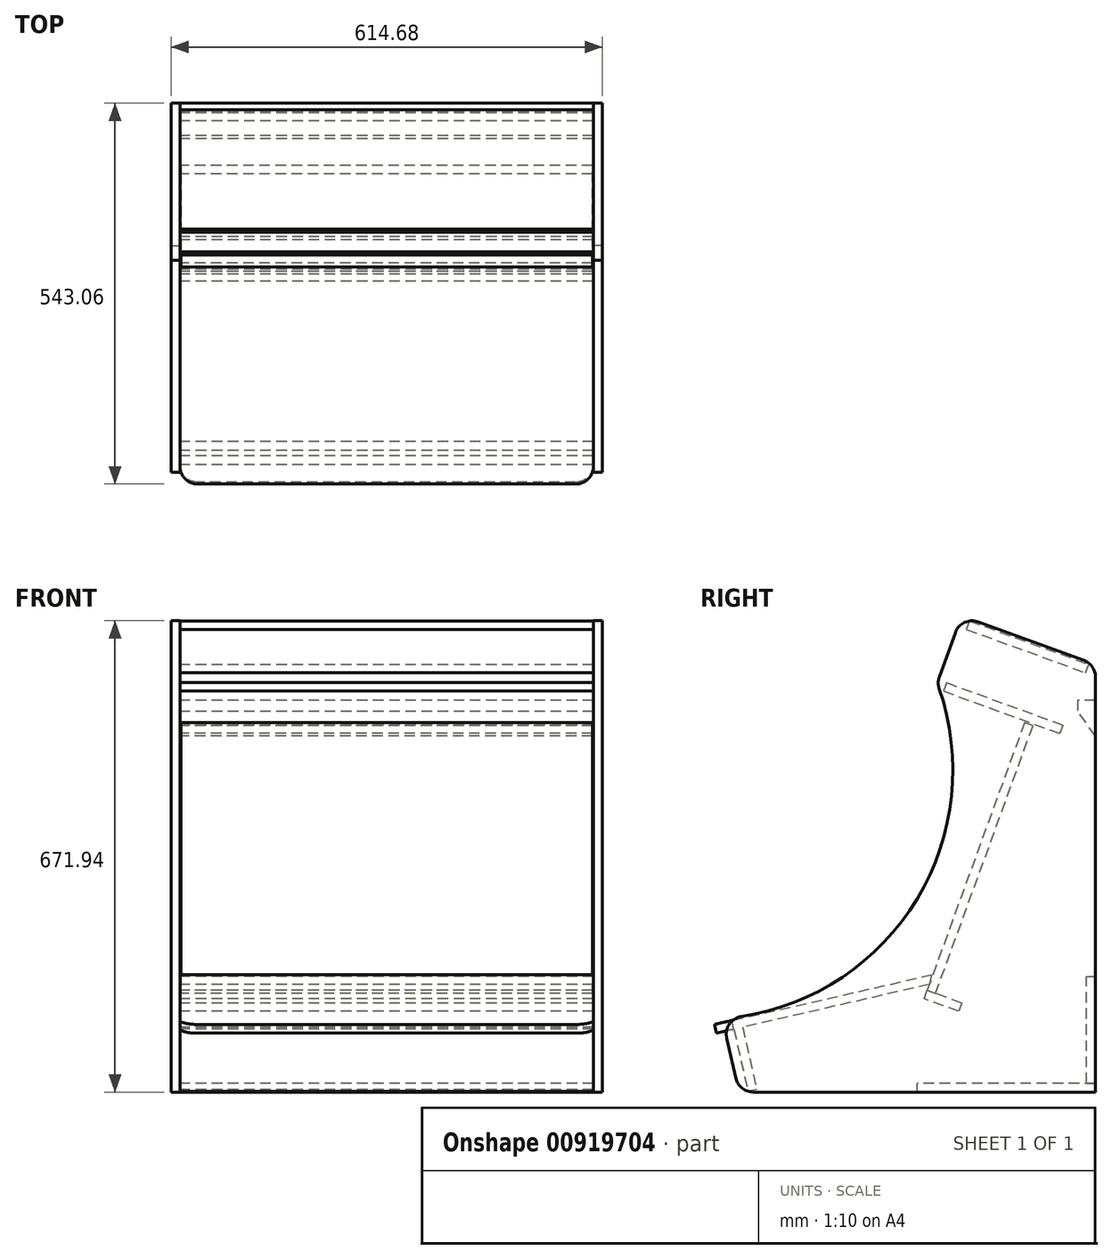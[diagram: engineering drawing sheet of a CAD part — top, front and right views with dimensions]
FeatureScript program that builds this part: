
annotation { "Feature Type Name" : "Feature", "Feature Type Description" : "" }
export const myFeature = defineFeature(function(context is Context, id is Id, definition is map)
    precondition{}
    {
        {
            var Q0;
            Q0=qCreatedBy(makeId("Right.planeOp"),FACE);
            var sketch = newSketch(context, id + "F0", { "sketchPlane" : qUnion([Q0])});
            skLineSegment(sketch, "E0", {"start": v(0, 0) * mm, "end": v(-508, 0) * mm});
            skLineSegment(sketch, "E1", {"start": v(0, 0) * mm, "end": v(0, 609.6) * mm});
            skLineSegment(sketch, "E2", {"start": v(0, 609.6) * mm, "end": v(-190.95, 679.1) * mm});
            skLineSegment(sketch, "E3", {"start": v(-190.95, 679.1) * mm, "end": v(-225.7, 583.63) * mm});
            skArc(sketch, "E4", {"start": v(-531.9, 104.58) * mm, "mid": v(-259.18, 267.64) * mm, "end": v(-225.7, 583.63) * mm});
            skLineSegment(sketch, "E5", {"start": v(-508, 0) * mm, "end": v(-531.9, 104.58) * mm});
            skLineSegment(sketch, "E6", {"start": v(-239.9, 144.98) * mm, "end": v(-100.9, 526.87) * mm, "construction": true});
            skLineSegment(sketch, "E7", {"start": v(-100.9, 526.87) * mm, "end": v(-51.5, 508.9) * mm, "construction": true});
            skLineSegment(sketch, "E8", {"start": v(-51.5, 508.9) * mm, "end": v(-190.5, 127) * mm, "construction": true});
            skLineSegment(sketch, "E9", {"start": v(-190.5, 127) * mm, "end": v(-239.9, 144.98) * mm, "construction": true});
            skLineSegment(sketch, "E10.0", {"start": v(-497.87, 12.7) * mm, "end": v(-516.3, 93.32) * mm, "construction": true});
            skLineSegment(sketch, "E10.1", {"start": v(-183.36, 662.82) * mm, "end": v(-212.17, 583.64) * mm, "construction": true});
            skLineSegment(sketch, "E10.2", {"start": v(-12.7, 600.7) * mm, "end": v(-183.36, 662.82) * mm, "construction": true});
            skArc(sketch, "E10.3", {"start": v(-516.3, 93.32) * mm, "mid": v(-245.82, 265.03) * mm, "end": v(-212.17, 583.64) * mm, "construction": true});
            skLineSegment(sketch, "E10.4", {"start": v(-12.7, 12.7) * mm, "end": v(-12.7, 600.7) * mm, "construction": true});
            skLineSegment(sketch, "E10.5", {"start": v(-12.7, 12.7) * mm, "end": v(-497.87, 12.7) * mm, "construction": true});
            skLineSegment(sketch, "E11", {"start": v(-528.79, 90.98) * mm, "end": v(-239.9, 144.98) * mm, "construction": true});
            skLineSegment(sketch, "E12.0", {"start": v(-518.63, 105.8) * mm, "end": v(-234.86, 158.85) * mm, "construction": true});
            skLineSegment(sketch, "E13", {"start": v(-253.62, 142.42) * mm, "end": v(-251.19, 129.41) * mm, "construction": true});
            skLineSegment(sketch, "E14", {"start": v(-251.19, 129.41) * mm, "end": v(-513.35, 80.4) * mm, "construction": true});
            skLineSegment(sketch, "E15", {"start": v(-190.5, 127) * mm, "end": v(-194.84, 115.07) * mm, "construction": true});
            skLineSegment(sketch, "E16", {"start": v(-194.84, 115.07) * mm, "end": v(-243.93, 132.93) * mm, "construction": true});
            skLineSegment(sketch, "E17", {"start": v(-243.93, 132.93) * mm, "end": v(-239.9, 144.98) * mm, "construction": true});
            skLineSegment(sketch, "E18", {"start": v(-212.17, 583.64) * mm, "end": v(-46.27, 523.26) * mm, "construction": true});
            skLineSegment(sketch, "E19", {"start": v(-46.27, 523.26) * mm, "end": v(-50.62, 511.32) * mm, "construction": true});
            skLineSegment(sketch, "E20", {"start": v(-216.52, 571.7) * mm, "end": v(-50.62, 511.32) * mm, "construction": true});
            skPoint(sketch, "E21.orphan", {"position": v(-51.5, 511.64) * mm});
            skLineSegment(sketch, "E22", {"start": v(-212.17, 583.64) * mm, "end": v(-216.52, 571.7) * mm, "construction": true});
            skLineSegment(sketch, "E23.bottom", {"start": v(0, 558.8) * mm, "end": v(-25.4, 558.8) * mm});
            skLineSegment(sketch, "E23.left", {"start": v(0, 558.8) * mm, "end": v(0, 508) * mm});
            skLineSegment(sketch, "E23.right", {"start": v(-25.4, 558.8) * mm, "end": v(-25.4, 542.58) * mm});
            skLineSegment(sketch, "E24", {"start": v(0, 508) * mm, "end": v(-25.4, 542.58) * mm});
            skPoint(sketch, "E25.orphan", {"position": v(-25.4, 526.36) * mm});
            skLineSegment(sketch, "E26", {"start": v(0, 0) * mm, "end": v(-408.6, 342.86) * mm, "construction": true});
            skCircle(sketch, "E27", {"center": v(-408.6, 342.86) * mm, "radius": 35.32 * mm, "construction": true});
            skLineSegment(sketch, "E28.1.2", {"start": v(-579.65, 9.55) * mm, "end": v(-544.9, 105.02) * mm});
            skArc(sketch, "E28.1.3", {"start": v(-238.7, 584.07) * mm, "mid": v(-511.42, 421) * mm, "end": v(-544.9, 105.02) * mm});
            skLineSegment(sketch, "E28.1.4", {"start": v(-262.6, 688.65) * mm, "end": v(-238.7, 584.07) * mm});
            skPoint(sketch, "E28.center", {"position": v(-385.3, 344.32) * mm});
            skSolve(sketch);
        }
        {
            var Q0;
            Q0=qCreatedBy(makeId("Right.planeOp"),FACE);
            cPlane(context, id + "F1", {"entities" : qUnion([Q0]), "cplaneType" : CPlaneType.OFFSET, "offset" : 294.64 * mm, "width" : 152.4 * mm, "height" : 152.4 * mm});
        }
        {
            var Q0;
            Q0=qCreatedBy(id+"F1.planeOp",FACE);
            var sketch = newSketch(context, id + "F2", { "sketchPlane" : qUnion([Q0])});
            skLineSegment(sketch, "E29.0", {"start": v(0, 0) * mm, "end": v(0, 609.6) * mm});
            skLineSegment(sketch, "E30.0", {"start": v(0, 609.6) * mm, "end": v(-190.95, 679.1) * mm});
            skPoint(sketch, "E31.0", {"position": v(-208.32, 631.36) * mm});
            skLineSegment(sketch, "E32.0", {"start": v(-190.95, 679.1) * mm, "end": v(-225.7, 583.63) * mm});
            skArc(sketch, "E33.0", {"start": v(-531.9, 104.58) * mm, "mid": v(-259.18, 267.64) * mm, "end": v(-225.7, 583.63) * mm});
            skPoint(sketch, "E34.0", {"position": v(-519.95, 52.29) * mm});
            skLineSegment(sketch, "E35.0", {"start": v(-508, 0) * mm, "end": v(-531.9, 104.58) * mm});
            skLineSegment(sketch, "E36.0", {"start": v(0, 0) * mm, "end": v(-508, 0) * mm});
            skSolve(sketch);
        }
        {
            var Q0;
            Q0 = qSketchRegion(id + "F2", true);
            extrude(context, id + "F3", {"entities" : qUnion([Q0]), "depth" : 12.7 * mm, "offsetDistance" : 25.4 * mm});
        }
        {
            var Q0;
            Q0=qCreatedBy(makeId("Right.planeOp"),FACE);
            cPlane(context, id + "F4", {"entities" : qUnion([Q0]), "cplaneType" : CPlaneType.OFFSET, "offset" : 294.64 * mm, "oppositeDirection" : true, "width" : 152.4 * mm, "height" : 152.4 * mm});
        }
        {
            var Q0;
            Q0=qCreatedBy(id+"F4.planeOp",FACE);
            var sketch = newSketch(context, id + "F5", { "sketchPlane" : qUnion([Q0])});
            skLineSegment(sketch, "E37.0", {"start": v(0, 0) * mm, "end": v(0, 609.6) * mm});
            skLineSegment(sketch, "E38.0", {"start": v(0, 609.6) * mm, "end": v(-190.95, 679.1) * mm});
            skLineSegment(sketch, "E39.0", {"start": v(-190.95, 679.1) * mm, "end": v(-225.7, 583.63) * mm});
            skArc(sketch, "E40.0", {"start": v(-531.9, 104.58) * mm, "mid": v(-259.18, 267.64) * mm, "end": v(-225.7, 583.63) * mm});
            skLineSegment(sketch, "E41.0", {"start": v(-508, 0) * mm, "end": v(-531.9, 104.58) * mm});
            skLineSegment(sketch, "E42.0", {"start": v(0, 0) * mm, "end": v(-508, 0) * mm});
            skSolve(sketch);
        }
        {
            var Q0;
            Q0=makeQuery(id+"F5.imprint","IMPRINT",FACE,{"disambiguationData":[TD([[makeQuery(id+"F5.imprint","IMPRINT",EDGE,{"derivedFrom":sQuery(id+"F5.wireOp",EDGE,"E37.0")}),1.0]])]});
            extrude(context, id + "F6", {"entities" : qUnion([Q0]), "oppositeDirection" : true, "depth" : 12.7 * mm, "offsetDistance" : 25.4 * mm});
        }
        {
            var Q0;
            Q0=makeQuery(id+"F6.opExtrude","SWEPT_EDGE",EDGE,{"disambiguationData":[OSD([sQuery(id+"F5.wireOp",EDGE,"E39.0"),sQuery(id+"F5.wireOp",EDGE,"E40.0")])]});
            var Q1;
            Q1=makeQuery(id+"F6.opExtrude","SWEPT_EDGE",EDGE,{"disambiguationData":[OSD([sQuery(id+"F5.wireOp",EDGE,"E38.0"),sQuery(id+"F5.wireOp",EDGE,"E39.0")])]});
            var Q2;
            Q2=makeQuery(id+"F3.opExtrude","SWEPT_EDGE",EDGE,{"disambiguationData":[OSD([sQuery(id+"F2.wireOp",EDGE,"E29.0"),sQuery(id+"F2.wireOp",EDGE,"E30.0")])]});
            var Q3;
            Q3=makeQuery(id+"F3.opExtrude","SWEPT_EDGE",EDGE,{"disambiguationData":[OSD([sQuery(id+"F2.wireOp",EDGE,"E30.0"),sQuery(id+"F2.wireOp",EDGE,"E32.0")])]});
            var Q4;
            Q4=makeQuery(id+"F6.opExtrude","SWEPT_EDGE",EDGE,{"disambiguationData":[OSD([sQuery(id+"F5.wireOp",EDGE,"E37.0"),sQuery(id+"F5.wireOp",EDGE,"E38.0")])]});
            var Q5;
            Q5=makeQuery(id+"F3.opExtrude","SWEPT_EDGE",EDGE,{"disambiguationData":[OSD([sQuery(id+"F2.wireOp",EDGE,"E32.0"),sQuery(id+"F2.wireOp",EDGE,"E33.0")])]});
            var Q6;
            Q6=makeQuery(id+"F6.opExtrude","SWEPT_EDGE",EDGE,{"disambiguationData":[OSD([sQuery(id+"F5.wireOp",EDGE,"E40.0"),sQuery(id+"F5.wireOp",EDGE,"E41.0")])]});
            var Q7;
            Q7=makeQuery(id+"F3.opExtrude","SWEPT_EDGE",EDGE,{"disambiguationData":[OSD([sQuery(id+"F2.wireOp",EDGE,"E33.0"),sQuery(id+"F2.wireOp",EDGE,"E35.0")])]});
            var Q8;
            Q8=makeQuery(id+"F3.opExtrude","SWEPT_EDGE",EDGE,{"disambiguationData":[OSD([sQuery(id+"F2.wireOp",EDGE,"E35.0"),sQuery(id+"F2.wireOp",EDGE,"E36.0")])]});
            var Q9;
            Q9=makeQuery(id+"F6.opExtrude","SWEPT_EDGE",EDGE,{"disambiguationData":[OSD([sQuery(id+"F5.wireOp",EDGE,"E41.0"),sQuery(id+"F5.wireOp",EDGE,"E42.0")])]});
            fillet(context, id + "F7", {"entities" : qUnion([Q0, Q1, Q2, Q3, Q4, Q5, Q6, Q7, Q8, Q9]), "radius" : 25.4 * mm, "tangentPropagation" : true, "allowEdgeOverflow" : false});
        }
        {
            var Q0;
            Q0=qCreatedBy(makeId("Right.planeOp"),FACE);
            var sketch = newSketch(context, id + "F8", { "sketchPlane" : qUnion([Q0])});
            skLineSegment(sketch, "E43.0", {"start": v(-495.25, 1.2) * mm, "end": v(-515.47, 89.7) * mm});
            skPoint(sketch, "E44.orphan", {"position": v(-497.87, 12.7) * mm});
            skLineSegment(sketch, "E45", {"start": v(-503.09, 92.54) * mm, "end": v(-515.47, 89.7) * mm});
            skLineSegment(sketch, "E46", {"start": v(-503.09, 92.54) * mm, "end": v(-482.7, 3.3) * mm});
            skLineSegment(sketch, "E47", {"start": v(-482.7, 3.3) * mm, "end": v(-495.25, 1.2) * mm});
            skPoint(sketch, "E48.orphan", {"position": v(-516.3, 93.32) * mm});
            skLineSegment(sketch, "E49", {"start": v(-515.47, 89.7) * mm, "end": v(-236.9, 153.36) * mm});
            skLineSegment(sketch, "E50.0", {"start": v(-518.3, 102.09) * mm, "end": v(-233.54, 167.15) * mm});
            skLineSegment(sketch, "E51", {"start": v(-518.3, 102.09) * mm, "end": v(-515.47, 89.7) * mm});
            skLineSegment(sketch, "E52", {"start": v(-233.54, 167.15) * mm, "end": v(-236.9, 153.36) * mm});
            skSolve(sketch);
        }
        {
            var Q0;
            Q0=makeQuery(id+"F8.imprint","IMPRINT",FACE,{"disambiguationData":[TD([[makeQuery(id+"F8.imprint","IMPRINT",EDGE,{"derivedFrom":sQuery(id+"F8.wireOp",EDGE,"E50.0")}),-1.0]])]});
            extrude(context, id + "F9", {"entities" : qUnion([Q0]), "endBound" : BoundingType.SYMMETRIC, "depth" : 589.28 * mm, "offsetDistance" : 25.4 * mm});
        }
        {
            var Q0;
            {var subQ0=sQuery(id+"F8.wireOp",EDGE,"E43.0");Q0=makeQuery(id+"F8.imprint","IMPRINT",FACE,{"disambiguationData":[TD([[makeQuery(id+"F8.imprint","IMPRINT",EDGE,{"derivedFrom":subQ0}),-1.0]])]});}
            extrude(context, id + "F10", {"entities" : qUnion([Q0]), "endBound" : BoundingType.SYMMETRIC, "depth" : 589.28 * mm, "offsetDistance" : 25.4 * mm});
        }
        {
            var Q0;
            Q0=makeQuery(id+"F0.imprint","IMPRINT",FACE,{"disambiguationData":[TD([[makeQuery(id+"F0.imprint","IMPRINT",EDGE,{"derivedFrom":sQuery(id+"F0.wireOp",EDGE,"E23.bottom")}),1.0]])]});
            extrude(context, id + "F11", {"entities" : qUnion([Q0]), "endBound" : BoundingType.SYMMETRIC, "depth" : 589.28 * mm, "offsetDistance" : 25.4 * mm});
        }
        {
            var Q0;
            Q0=makeQuery(id+"F9.opExtrude","SWEPT_FACE",FACE,{"disambiguationData":[OSD([sQuery(id+"F8.wireOp",EDGE,"E51")])]});
            extrude(context, id + "F12", {"entities" : qUnion([Q0]), "operationType" : NewBodyOperationType.ADD, "depth" : 25.4 * mm, "offsetDistance" : 25.4 * mm});
        }
        {
            var Q0;
            {var subQ0=sQuery(id+"F8.wireOp",EDGE,"E51");Q0=makeQuery(id+"F12.opExtrude","CAP_EDGE",EDGE,{"disambiguationData":[OSD([subQ0]),TDD([makeQuery(id+"F9.opExtrude","CAP_EDGE",EDGE,{"disambiguationData":[OSD([subQ0])],"isStart":true})])],"isStart":false});}
            var Q1;
            {var subQ0=sQuery(id+"F8.wireOp",EDGE,"E51");Q1=makeQuery(id+"F12.opExtrude","CAP_EDGE",EDGE,{"disambiguationData":[OSD([subQ0]),TDD([makeQuery(id+"F9.opExtrude","CAP_EDGE",EDGE,{"disambiguationData":[OSD([subQ0])],"isStart":false})])],"isStart":false});}
            fillet(context, id + "F13", {"entities" : qUnion([Q0, Q1]), "radius" : 25.4 * mm, "tangentPropagation" : true, "allowEdgeOverflow" : false});
        }
        {
            var Q0;
            Q0=qCreatedBy(makeId("Right.planeOp"),FACE);
            var sketch = newSketch(context, id + "F14", { "sketchPlane" : qUnion([Q0])});
            skLineSegment(sketch, "E53.0", {"start": v(-16.71, 615.68) * mm, "end": v(-167.08, 670.41) * mm});
            skLineSegment(sketch, "E54", {"start": v(-179.5, 671.56) * mm, "end": v(-183.85, 659.62) * mm});
            skLineSegment(sketch, "E55", {"start": v(-183.85, 659.62) * mm, "end": v(-13.79, 597.72) * mm});
            skLineSegment(sketch, "E56", {"start": v(-13.79, 597.72) * mm, "end": v(-9.44, 609.66) * mm});
            skArc(sketch, "E57.0", {"start": v(-167.08, 670.41) * mm, "mid": v(-186.5, 669.56) * mm, "end": v(-199.63, 655.23) * mm, "construction": true});
            skPoint(sketch, "E58.orphan", {"position": v(-190.95, 679.1) * mm});
            skArc(sketch, "E59.0", {"start": v(0, 591.81) * mm, "mid": v(-4.6, 606.38) * mm, "end": v(-16.71, 615.68) * mm, "construction": true});
            skPoint(sketch, "E60.orphan", {"position": v(0, 609.6) * mm});
            skLineSegment(sketch, "E61", {"start": v(-179.5, 671.56) * mm, "end": v(-9.44, 609.66) * mm});
            skSolve(sketch);
        }
        {
            var Q0;
            Q0 = qSketchRegion(id + "F14", true);
            extrude(context, id + "F15", {"entities" : qUnion([Q0]), "endBound" : BoundingType.SYMMETRIC, "depth" : 589.28 * mm, "offsetDistance" : 25.4 * mm});
        }
        {
            var Q0;
            Q0=qCreatedBy(makeId("Right.planeOp"),FACE);
            var sketch = newSketch(context, id + "F16", { "sketchPlane" : qUnion([Q0])});
            skLineSegment(sketch, "E62.0", {"start": v(-212.17, 583.64) * mm, "end": v(-46.27, 523.26) * mm});
            skLineSegment(sketch, "E63.0", {"start": v(-216.52, 571.7) * mm, "end": v(-50.62, 511.32) * mm});
            skLineSegment(sketch, "E64.0", {"start": v(-212.17, 583.64) * mm, "end": v(-216.52, 571.7) * mm});
            skLineSegment(sketch, "E65.0", {"start": v(-46.27, 523.26) * mm, "end": v(-50.62, 511.32) * mm});
            skSolve(sketch);
        }
        {
            var Q0;
            Q0=makeQuery(id+"F16.imprint","IMPRINT",FACE,{"disambiguationData":[TD([[makeQuery(id+"F16.imprint","IMPRINT",EDGE,{"derivedFrom":sQuery(id+"F16.wireOp",EDGE,"E62.0")}),-1.0]])]});
            extrude(context, id + "F17", {"entities" : qUnion([Q0]), "endBound" : BoundingType.SYMMETRIC, "depth" : 589.28 * mm, "offsetDistance" : 25.4 * mm});
        }
        {
            var Q0;
            Q0=qCreatedBy(makeId("Right.planeOp"),FACE);
            var sketch = newSketch(context, id + "F18", { "sketchPlane" : qUnion([Q0])});
            skLineSegment(sketch, "E66.bottom", {"start": v(0, 0) * mm, "end": v(-254, 0) * mm});
            skLineSegment(sketch, "E66.top", {"start": v(0, 12.7) * mm, "end": v(-254, 12.7) * mm});
            skLineSegment(sketch, "E66.left", {"start": v(0, 0) * mm, "end": v(0, 12.7) * mm});
            skLineSegment(sketch, "E66.right", {"start": v(-254, 0) * mm, "end": v(-254, 12.7) * mm});
            skSolve(sketch);
        }
        {
            var Q0;
            Q0 = qSketchRegion(id + "F18", true);
            extrude(context, id + "F19", {"entities" : qUnion([Q0]), "endBound" : BoundingType.SYMMETRIC, "depth" : 589.28 * mm, "offsetDistance" : 25.4 * mm});
        }
        {
            var Q0;
            Q0=qCreatedBy(makeId("Right.planeOp"),FACE);
            var sketch = newSketch(context, id + "F20", { "sketchPlane" : qUnion([Q0])});
            skPoint(sketch, "E67.0", {"position": v(-12.7, 12.7) * mm});
            skLineSegment(sketch, "E68.bottom", {"start": v(-12.7, 12.7) * mm, "end": v(0, 12.7) * mm});
            skLineSegment(sketch, "E68.top", {"start": v(-12.7, 165.1) * mm, "end": v(0, 165.1) * mm});
            skLineSegment(sketch, "E68.left", {"start": v(-12.7, 12.7) * mm, "end": v(-12.7, 165.1) * mm});
            skLineSegment(sketch, "E68.right", {"start": v(0, 12.7) * mm, "end": v(0, 165.1) * mm});
            skSolve(sketch);
        }
        {
            var Q0;
            Q0 = qSketchRegion(id + "F20", true);
            extrude(context, id + "F21", {"entities" : qUnion([Q0]), "endBound" : BoundingType.SYMMETRIC, "depth" : 589.28 * mm, "offsetDistance" : 25.4 * mm});
        }
        {
            var Q0;
            Q0=qCreatedBy(makeId("Right.planeOp"),FACE);
            var sketch = newSketch(context, id + "F22", { "sketchPlane" : qUnion([Q0])});
            skPoint(sketch, "E69.0", {"position": v(-100.9, 526.87) * mm});
            skPoint(sketch, "E70.0", {"position": v(-239.9, 144.98) * mm});
            skLineSegment(sketch, "E71", {"start": v(-100.9, 526.87) * mm, "end": v(-239.9, 144.98) * mm});
            skLineSegment(sketch, "E72", {"start": v(-239.9, 144.98) * mm, "end": v(-227.97, 140.64) * mm});
            skLineSegment(sketch, "E73", {"start": v(-227.97, 140.64) * mm, "end": v(-88.97, 522.53) * mm});
            skLineSegment(sketch, "E74", {"start": v(-88.97, 522.53) * mm, "end": v(-100.9, 526.87) * mm});
            skSolve(sketch);
        }
        {
            var Q0;
            Q0 = qSketchRegion(id + "F22", true);
            extrude(context, id + "F23", {"entities" : qUnion([Q0]), "endBound" : BoundingType.SYMMETRIC, "depth" : 586.74 * mm, "offsetDistance" : 25.4 * mm});
        }
        {
            var Q0;
            Q0=qCreatedBy(makeId("Right.planeOp"),FACE);
            var sketch = newSketch(context, id + "F24", { "sketchPlane" : qUnion([Q0])});
            skLineSegment(sketch, "E75.0", {"start": v(-190.5, 127) * mm, "end": v(-239.9, 144.98) * mm});
            skLineSegment(sketch, "E76.0", {"start": v(-194.84, 115.07) * mm, "end": v(-243.93, 132.93) * mm});
            skLineSegment(sketch, "E77.0", {"start": v(-190.5, 127) * mm, "end": v(-194.84, 115.07) * mm});
            skLineSegment(sketch, "E78.0", {"start": v(-243.93, 132.93) * mm, "end": v(-239.9, 144.98) * mm});
            skSolve(sketch);
        }
        {
            var Q0;
            Q0=makeQuery(id+"F24.imprint","IMPRINT",FACE,{"disambiguationData":[TD([[makeQuery(id+"F24.imprint","IMPRINT",EDGE,{"derivedFrom":sQuery(id+"F24.wireOp",EDGE,"E75.0")}),1.0]])]});
            extrude(context, id + "F25", {"entities" : qUnion([Q0]), "endBound" : BoundingType.SYMMETRIC, "depth" : 589.28 * mm, "offsetDistance" : 25.4 * mm});
        }
    });
